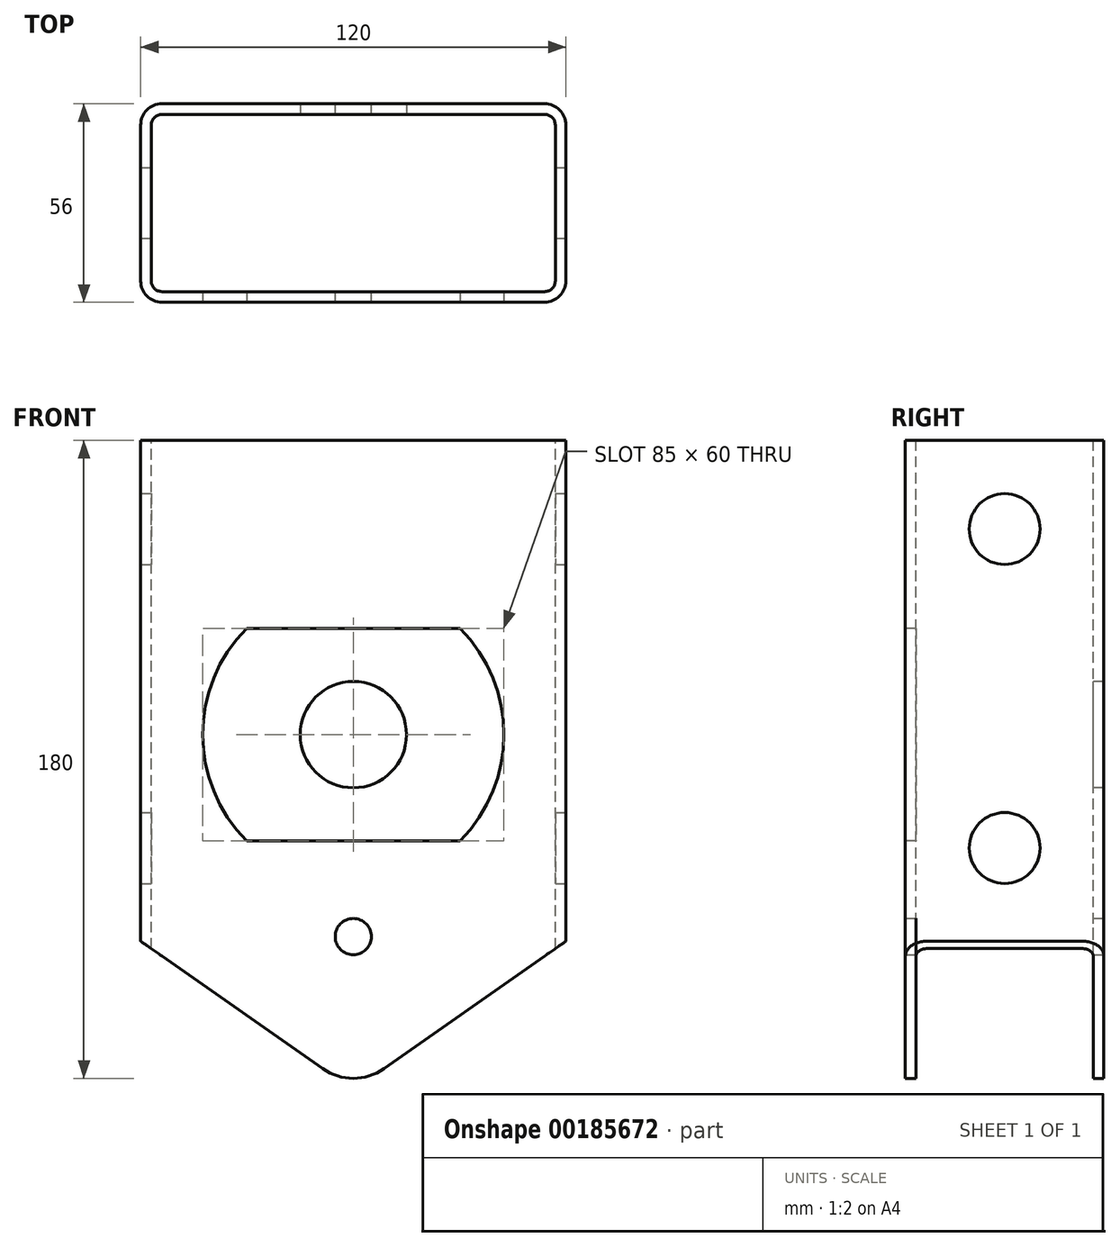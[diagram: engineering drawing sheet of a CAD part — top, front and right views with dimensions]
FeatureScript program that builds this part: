
annotation { "Feature Type Name" : "Feature", "Feature Type Description" : "" }
export const myFeature = defineFeature(function(context is Context, id is Id, definition is map)
    precondition{}
    {
        {
            var Q0;
            Q0=qCreatedBy(makeId("Front.planeOp"),FACE);
            var sketch = newSketch(context, id + "F0", { "sketchPlane" : qUnion([Q0])});
            skLineSegment(sketch, "E0.bottom", {"start": v(-60, 100) * mm, "end": v(60, 100) * mm});
            skLineSegment(sketch, "E0.left", {"start": v(-60, 100) * mm, "end": v(-60, -41.3) * mm});
            skLineSegment(sketch, "E0.right", {"start": v(60, 100) * mm, "end": v(60, -41.3) * mm});
            skArc(sketch, "E1", {"start": v(-8.6, -77.29) * mm, "mid": v(0, -80) * mm, "end": v(8.6, -77.29) * mm});
            skPoint(sketch, "E1.centerSnap0", {"position": v(0, -65) * mm});
            skLineSegment(sketch, "E2", {"start": v(60, -41.3) * mm, "end": v(8.6, -77.29) * mm});
            skLineSegment(sketch, "E3", {"start": v(-8.6, -77.29) * mm, "end": v(-60, -41.3) * mm});
            skPoint(sketch, "E4.orphan", {"position": v(0, -83.31) * mm});
            skCircle(sketch, "E5", {"center": v(0, -40) * mm, "radius": 5.1 * mm});
            skSolve(sketch);
        }
        {
            var Q0;
            Q0 = qSketchRegion(id + "F0", true);
            extrude(context, id + "F1", {"entities" : qUnion([Q0]), "depth" : 56 * mm});
        }
        {
            var Q0;
            Q0=makeQuery(id+"F1.opExtrude","SWEPT_FACE",FACE,{"disambiguationData":[OSD([sQuery(id+"F0.wireOp",EDGE,"E0.bottom")])]});
            var sketch = newSketch(context, id + "F2", { "sketchPlane" : qUnion([Q0])});
            skLineSegment(sketch, "E6.bottom", {"start": v(-54, -3) * mm, "end": v(54, -3) * mm});
            skLineSegment(sketch, "E6.top", {"start": v(-54, -53) * mm, "end": v(54, -53) * mm});
            skLineSegment(sketch, "E6.left", {"start": v(-57, -6) * mm, "end": v(-57, -50) * mm});
            skLineSegment(sketch, "E6.right", {"start": v(57, -6) * mm, "end": v(57, -50) * mm});
            skPoint(sketch, "E7.visualSharp", {"position": v(57, -3) * mm});
            skArc(sketch, "E7.filletArc", {"start": v(57, -6) * mm, "mid": v(56.12, -3.88) * mm, "end": v(54, -3) * mm});
            skPoint(sketch, "E8.visualSharp", {"position": v(57, -53) * mm});
            skArc(sketch, "E8.filletArc", {"start": v(54, -53) * mm, "mid": v(56.12, -52.12) * mm, "end": v(57, -50) * mm});
            skPoint(sketch, "E9.visualSharp", {"position": v(-57, -3) * mm});
            skArc(sketch, "E9.filletArc", {"start": v(-54, -3) * mm, "mid": v(-56.12, -3.88) * mm, "end": v(-57, -6) * mm});
            skPoint(sketch, "E10.visualSharp", {"position": v(-57, -53) * mm});
            skArc(sketch, "E10.filletArc", {"start": v(-57, -50) * mm, "mid": v(-56.12, -52.12) * mm, "end": v(-54, -53) * mm});
            skSolve(sketch);
        }
        {
            var Q0;
            Q0 = qSketchRegion(id + "F2", true);
            extrude(context, id + "F3", {"entities" : qUnion([Q0]), "operationType" : NewBodyOperationType.REMOVE, "endBound" : BoundingType.UP_TO_NEXT, "oppositeDirection" : true, "depth" : 25 * mm});
        }
        {
            var Q0;
            Q0=makeQuery(id+"F1.opExtrude","CAP_FACE",FACE,{"disambiguationData":[OSD([sQuery(id+"F0.wireOp",EDGE,"E0.bottom"),sQuery(id+"F0.wireOp",EDGE,"E0.left"),sQuery(id+"F0.wireOp",EDGE,"E0.right"),sQuery(id+"F0.wireOp",EDGE,"E1"),sQuery(id+"F0.wireOp",EDGE,"E2"),sQuery(id+"F0.wireOp",EDGE,"E3"),sQuery(id+"F0.wireOp",EDGE,"E5")])],"isStart":false});
            var sketch = newSketch(context, id + "F4", { "sketchPlane" : qUnion([Q0])});
            skArc(sketch, "E11", {"start": v(-30.1, 47) * mm, "mid": v(-42.5, 17) * mm, "end": v(-30.1, -13) * mm});
            skLineSegment(sketch, "E12", {"start": v(-30.1, 47) * mm, "end": v(30.1, 47) * mm});
            skLineSegment(sketch, "E13", {"start": v(30.1, -13) * mm, "end": v(-30.1, -13) * mm});
            skArc(sketch, "E14.trimOffspring", {"start": v(30.1, -13) * mm, "mid": v(42.5, 17) * mm, "end": v(30.1, 47) * mm});
            skSolve(sketch);
        }
        {
            var Q0;
            Q0 = qSketchRegion(id + "F4", true);
            extrude(context, id + "F5", {"entities" : qUnion([Q0]), "operationType" : NewBodyOperationType.REMOVE, "endBound" : BoundingType.UP_TO_NEXT, "oppositeDirection" : true, "depth" : 25 * mm});
        }
        {
            var Q0;
            Q0=makeQuery(id+"F3.boolean.opBoolean","COPY",FACE,{"derivedFrom":makeQuery(id+"F3.opExtrude","SWEPT_FACE",FACE,{"disambiguationData":[OSD([sQuery(id+"F2.wireOp",EDGE,"E6.bottom")])]})});
            var sketch = newSketch(context, id + "F6", { "sketchPlane" : qUnion([Q0])});
            skCircle(sketch, "E15", {"center": v(0, 17) * mm, "radius": 15 * mm});
            skSolve(sketch);
        }
        {
            var Q0;
            Q0 = qSketchRegion(id + "F6", true);
            extrude(context, id + "F7", {"entities" : qUnion([Q0]), "operationType" : NewBodyOperationType.REMOVE, "oppositeDirection" : true, "depth" : 25 * mm});
        }
        {
            var Q0;
            Q0=makeQuery(id+"F1.opExtrude","SWEPT_FACE",FACE,{"disambiguationData":[OSD([sQuery(id+"F0.wireOp",EDGE,"E0.right")])]});
            var sketch = newSketch(context, id + "F8", { "sketchPlane" : qUnion([Q0])});
            skCircle(sketch, "E16", {"center": v(-28, 75) * mm, "radius": 10 * mm});
            skCircle(sketch, "E17", {"center": v(-28, -15) * mm, "radius": 10 * mm});
            skSolve(sketch);
        }
        {
            var Q0;
            Q0 = qSketchRegion(id + "F8", true);
            extrude(context, id + "F9", {"entities" : qUnion([Q0]), "operationType" : NewBodyOperationType.REMOVE, "endBound" : BoundingType.THROUGH_ALL, "oppositeDirection" : true, "depth" : 25 * mm});
        }
        {
            var Q0;
            Q0=makeQuery(id+"F1.opExtrude","CAP_EDGE",EDGE,{"disambiguationData":[OSD([sQuery(id+"F0.wireOp",EDGE,"E0.left")])],"isStart":false});
            var Q1;
            Q1=makeQuery(id+"F1.opExtrude","CAP_EDGE",EDGE,{"disambiguationData":[OSD([sQuery(id+"F0.wireOp",EDGE,"E0.right")])],"isStart":false});
            var Q2;
            Q2=makeQuery(id+"F1.opExtrude","CAP_EDGE",EDGE,{"disambiguationData":[OSD([sQuery(id+"F0.wireOp",EDGE,"E0.left")])],"isStart":true});
            var Q3;
            Q3=makeQuery(id+"F1.opExtrude","CAP_EDGE",EDGE,{"disambiguationData":[OSD([sQuery(id+"F0.wireOp",EDGE,"E0.right")])],"isStart":true});
            fillet(context, id + "F10", {"entities" : qUnion([Q0, Q1, Q2, Q3]), "radius" : 6 * mm, "tangentPropagation" : true, "allowEdgeOverflow" : false});
        }
    });
